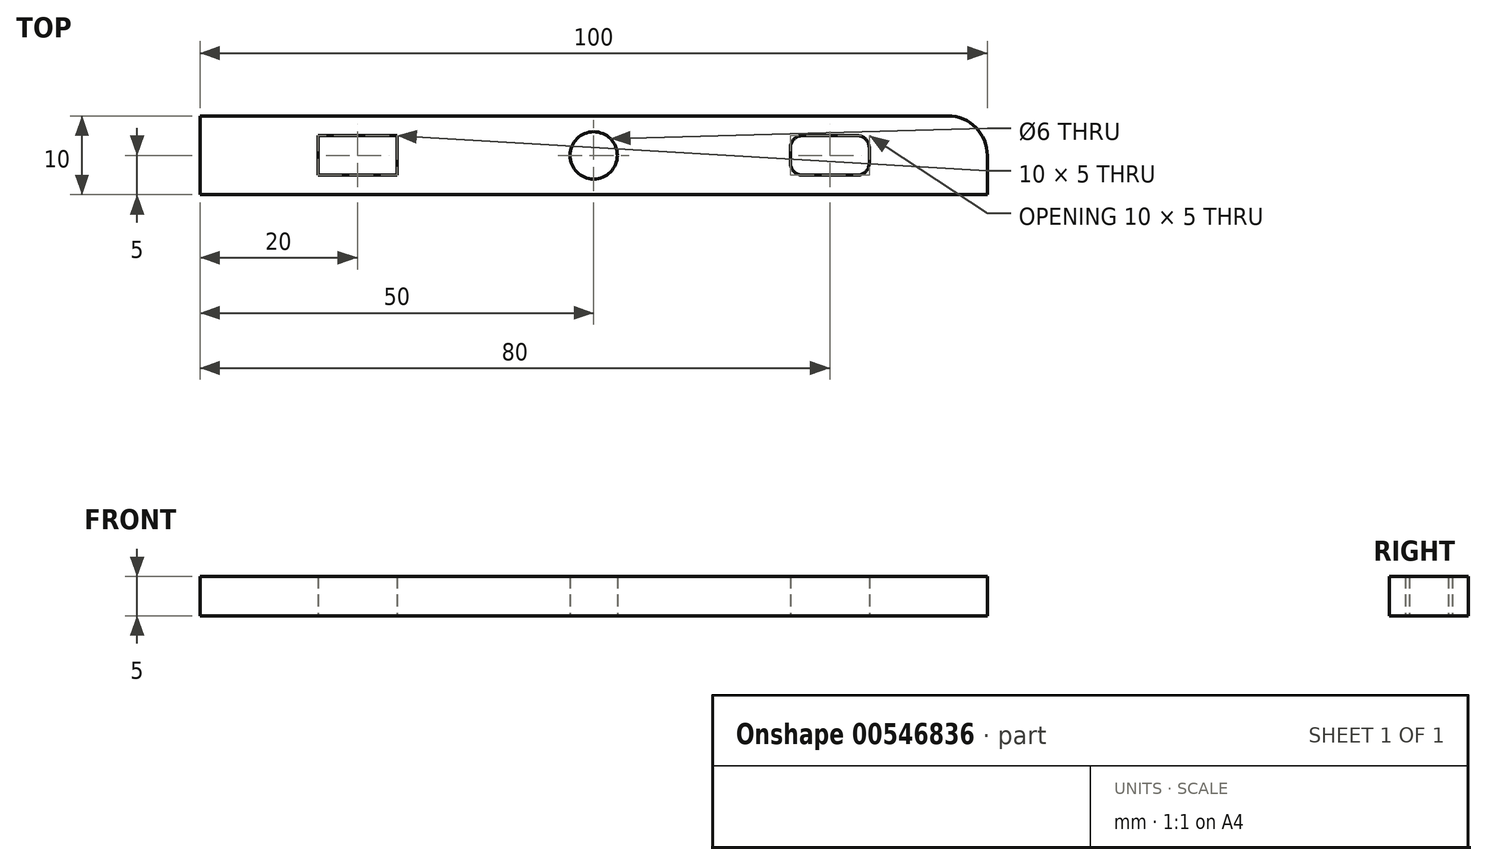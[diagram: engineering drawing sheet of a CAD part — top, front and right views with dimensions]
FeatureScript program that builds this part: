
annotation { "Feature Type Name" : "Feature", "Feature Type Description" : "" }
export const myFeature = defineFeature(function(context is Context, id is Id, definition is map)
    precondition{}
    {
        {
            var Q0;
            Q0=qCreatedBy(makeId("Top.planeOp"),FACE);
            var sketch = newSketch(context, id + "F0", { "sketchPlane" : qUnion([Q0])});
            skLineSegment(sketch, "E0.bottom", {"start": v(50, -5) * mm, "end": v(-50, -5) * mm});
            skLineSegment(sketch, "E0.top", {"start": v(45, 5) * mm, "end": v(-50, 5) * mm});
            skLineSegment(sketch, "E0.left", {"start": v(50, -5) * mm, "end": v(50, 0) * mm});
            skLineSegment(sketch, "E0.right", {"start": v(-50, -5) * mm, "end": v(-50, 5) * mm});
            skPoint(sketch, "E0.middle", {"position": v(0, 0) * mm});
            skCircle(sketch, "E1", {"center": v(0, 0) * mm, "radius": 3 * mm});
            skPoint(sketch, "E2.visualSharp", {"position": v(50, 5) * mm});
            skArc(sketch, "E2.filletArc", {"start": v(50, 0) * mm, "mid": v(48.54, 3.54) * mm, "end": v(45, 5) * mm});
            skLineSegment(sketch, "E3.bottom", {"start": v(-25, -2.5) * mm, "end": v(-35, -2.5) * mm});
            skLineSegment(sketch, "E3.top", {"start": v(-25, 2.5) * mm, "end": v(-35, 2.5) * mm});
            skLineSegment(sketch, "E3.left", {"start": v(-25, -2.5) * mm, "end": v(-25, 2.5) * mm});
            skLineSegment(sketch, "E3.right", {"start": v(-35, -2.5) * mm, "end": v(-35, 2.5) * mm});
            skPoint(sketch, "E3.middle", {"position": v(-30, 0) * mm});
            skLineSegment(sketch, "E4.bottom", {"start": v(33.5, -2.5) * mm, "end": v(26.5, -2.5) * mm});
            skLineSegment(sketch, "E4.top", {"start": v(33.5, 2.5) * mm, "end": v(26.5, 2.5) * mm});
            skLineSegment(sketch, "E4.left", {"start": v(35, -1) * mm, "end": v(35, 1) * mm});
            skLineSegment(sketch, "E4.right", {"start": v(25, -1) * mm, "end": v(25, 1) * mm});
            skPoint(sketch, "E4.middle", {"position": v(30, 0) * mm});
            skPoint(sketch, "E5.visualSharp", {"position": v(25, 2.5) * mm});
            skArc(sketch, "E5.filletArc", {"start": v(26.5, 2.5) * mm, "mid": v(25.44, 2.06) * mm, "end": v(25, 1) * mm});
            skPoint(sketch, "E6.visualSharp", {"position": v(25, -2.5) * mm});
            skArc(sketch, "E6.filletArc", {"start": v(25, -1) * mm, "mid": v(25.44, -2.06) * mm, "end": v(26.5, -2.5) * mm});
            skPoint(sketch, "E7.visualSharp", {"position": v(35, -2.5) * mm});
            skArc(sketch, "E7.filletArc", {"start": v(33.5, -2.5) * mm, "mid": v(34.56, -2.06) * mm, "end": v(35, -1) * mm});
            skPoint(sketch, "E8.visualSharp", {"position": v(35, 2.5) * mm});
            skArc(sketch, "E8.filletArc", {"start": v(35, 1) * mm, "mid": v(34.56, 2.06) * mm, "end": v(33.5, 2.5) * mm});
            skSolve(sketch);
        }
        {
            var Q0;
            Q0 = qSketchRegion(id + "F0", true);
            extrude(context, id + "F1", {"entities" : qUnion([Q0]), "depth" : 5 * mm, "offsetDistance" : 25 * mm});
        }
    });
